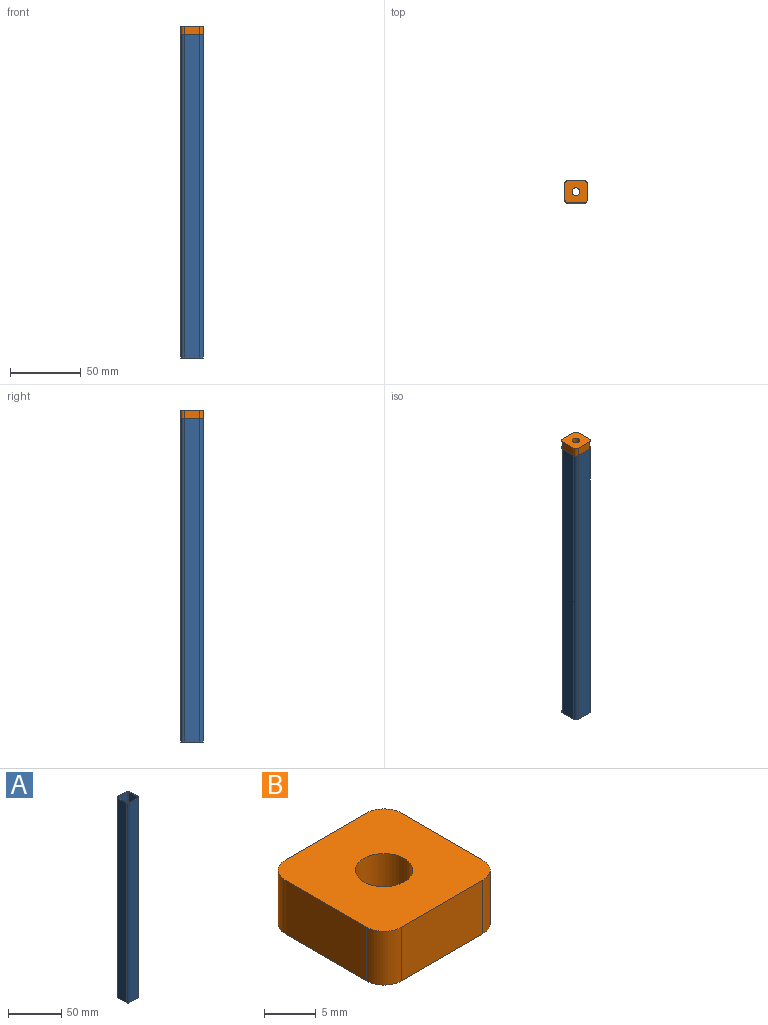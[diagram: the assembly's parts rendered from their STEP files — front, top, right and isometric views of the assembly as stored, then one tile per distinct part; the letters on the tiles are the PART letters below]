
ASSEMBLY  parts=2 mates=1
PART A: 18 faces, bbox 15.9x15.9x228.6 mm
  f0: plane 228.6x11.14mm, normal (1,0,0), area 2545.5mm2, adj f1,f15,f16,f17
  f1: cylinder r=2.37mm len=228.6mm, axis (0,0,-1), area 851mm2, adj f0,f2,f16,f17
  f2: plane 228.6x11.14mm, normal (0,1,0), area 2545.5mm2, adj f1,f3,f16,f17
  f3: cylinder r=2.37mm len=228.6mm, axis (0,0,-1), area 851mm2, adj f2,f4,f16,f17
  f4: plane 228.6x11.14mm, normal (-1,0,0), area 2545.5mm2, adj f3,f5,f16,f17
  f5: cylinder r=2.37mm len=228.6mm, axis (0,0,-1), area 851mm2, adj f4,f6,f16,f17
  f6: plane 228.6x11.14mm, normal (0,-1,0), area 2545.5mm2, adj f5,f15,f16,f17
  f7: plane 228.6x11.14mm, normal (0,-1,0), area 2545.5mm2, adj f8,f14,f16,f17
  f8: cylinder r=1.13mm len=228.6mm, axis (0,0,-1), area 404mm2, adj f7,f9,f16,f17
  f9: plane 228.6x11.14mm, normal (-1,0,0), area 2545.5mm2, adj f8,f10,f16,f17
  f10: cylinder r=1.13mm len=228.6mm, axis (0,0,-1), area 404mm2, adj f9,f11,f16,f17
  f11: plane 228.6x11.14mm, normal (0,1,0), area 2545.5mm2, adj f10,f12,f16,f17
  f12: cylinder r=1.13mm len=228.6mm, axis (0,0,-1), area 404mm2, adj f11,f13,f16,f17
  f13: plane 228.6x11.14mm, normal (1,0,0), area 2545.5mm2, adj f12,f14,f16,f17
  f14: cylinder r=1.13mm len=228.6mm, axis (0,0,-1), area 404mm2, adj f7,f13,f16,f17
  f15: cylinder r=2.37mm len=228.6mm, axis (0,0,-1), area 851mm2, adj f0,f6,f16,f17
  f16: plane 15.88x15.88mm, normal (0,0,1), area 69.1mm2, adj f0,f1,f2,f3,f4,f5,f6,f7
  f17: plane 15.88x15.88mm, normal (0,0,-1), area 69.1mm2, adj f0,f1,f2,f3,f4,f5,f6,f7
PART B: 11 faces, bbox 15.9x15.9x6.4 mm
  f0: plane 11.11x6.35mm, normal (1,0,0), area 70.6mm2, adj f1,f8,f9,f10
  f1: cylinder r=2.38mm len=6.35mm, axis (0,0,-1), area 23.8mm2, adj f0,f2,f9,f10
  f2: plane 11.11x6.35mm, normal (0,1,0), area 70.6mm2, adj f1,f3,f9,f10
  f3: cylinder r=2.38mm len=6.35mm, axis (0,0,-1), area 23.8mm2, adj f2,f4,f9,f10
  f4: plane 11.11x6.35mm, normal (-1,0,0), area 70.6mm2, adj f3,f5,f9,f10
  f5: cylinder r=2.38mm len=6.35mm, axis (0,0,-1), area 23.8mm2, adj f4,f6,f9,f10
  f6: plane 11.11x6.35mm, normal (0,-1,0), area 70.6mm2, adj f5,f8,f9,f10
  f7: cylinder r=2.77mm len=6.35mm, axis (0,0,-1), area 110.6mm2, adj f9,f10
  f8: cylinder r=2.38mm len=6.35mm, axis (0,0,-1), area 23.8mm2, adj f0,f6,f9,f10
  f9: plane 15.88x15.88mm, normal (0,0,1), area 223mm2, adj f0,f1,f2,f3,f4,f5,f6,f7
  f10: plane 15.88x15.88mm, normal (0,0,-1), area 223mm2, adj f0,f1,f2,f3,f4,f5,f6,f7
PLACE A at identity fixed
PLACE B t=(0.01,0.01,228.6)mm
MATE fastened A.f1 <-> B.f1  axis (0,0,1) through (5.57,5.57,228.6)mm
